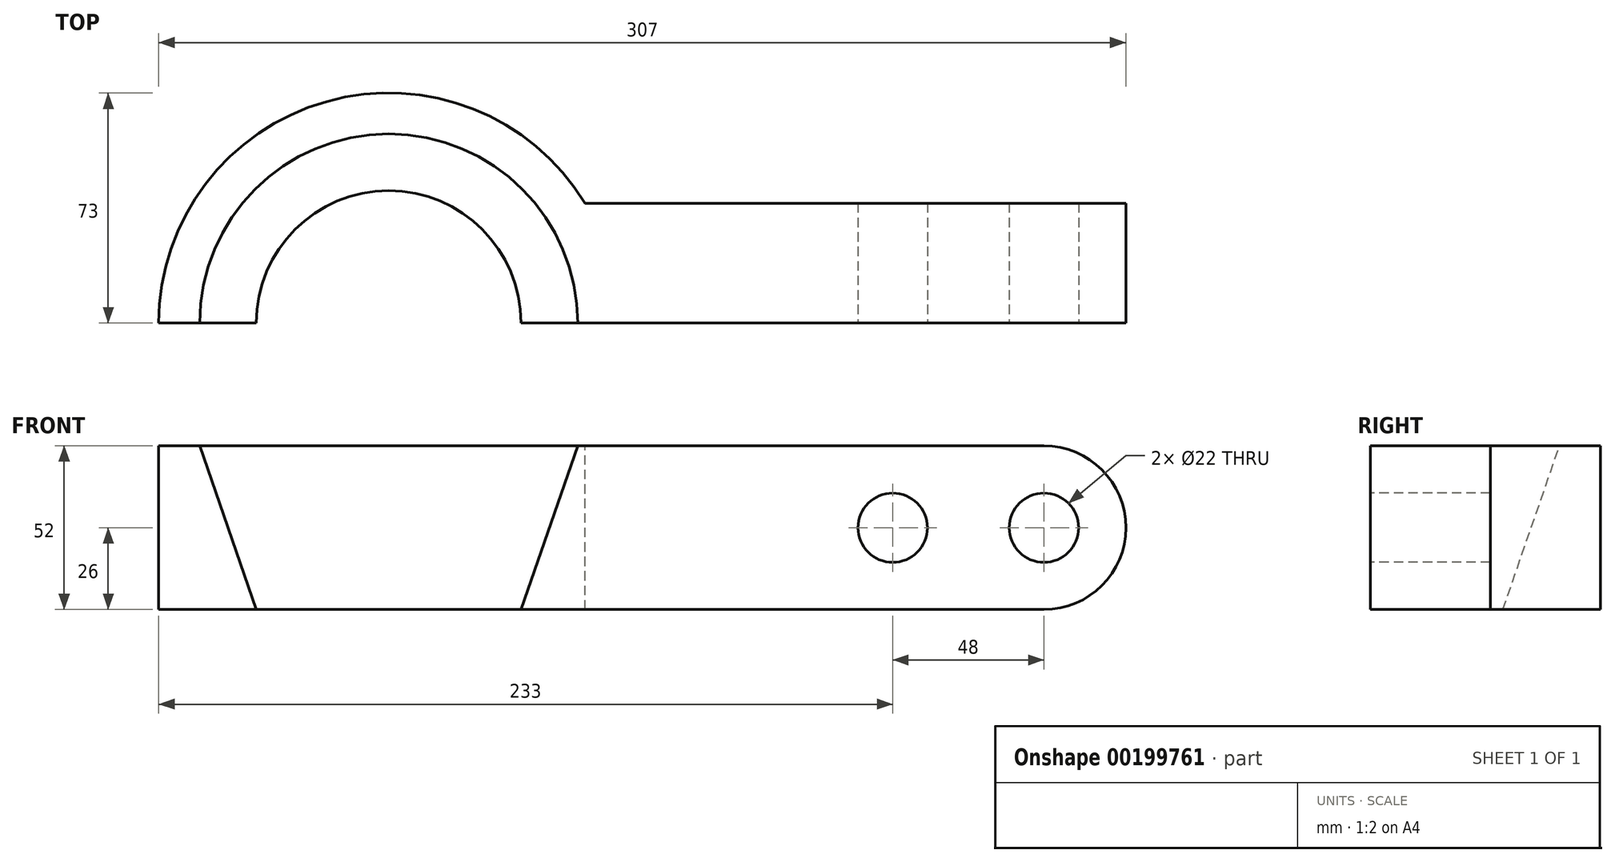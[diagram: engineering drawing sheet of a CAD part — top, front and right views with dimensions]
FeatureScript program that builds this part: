
annotation { "Feature Type Name" : "Feature", "Feature Type Description" : "" }
export const myFeature = defineFeature(function(context is Context, id is Id, definition is map)
    precondition{}
    {
        {
            var Q0;
            Q0=qCreatedBy(makeId("Front.planeOp"),FACE);
            var sketch = newSketch(context, id + "F0", { "sketchPlane" : qUnion([Q0])});
            skLineSegment(sketch, "E0", {"start": v(-73, 0) * mm, "end": v(-73, 52) * mm});
            skLineSegment(sketch, "E1", {"start": v(-73, 52) * mm, "end": v(-60, 52) * mm});
            skLineSegment(sketch, "E2", {"start": v(-60, 52) * mm, "end": v(-42, 0) * mm});
            skLineSegment(sketch, "E3", {"start": v(-42, 0) * mm, "end": v(-73, 0) * mm});
            skLineSegment(sketch, "E4", {"start": v(0, 0) * mm, "end": v(0, 74.37) * mm, "construction": true});
            skSolve(sketch);
        }
        {
            var Q0;
            Q0=qCreatedBy(makeId("Front.planeOp"),FACE);
            var sketch = newSketch(context, id + "F1", { "sketchPlane" : qUnion([Q0])});
            skLineSegment(sketch, "E5", {"start": v(0, 0) * mm, "end": v(0, 72.86) * mm});
            skSolve(sketch);
        }
        {
            var Q0;
            Q0=makeQuery(id+"F0.imprint","IMPRINT",FACE,{"disambiguationData":[TD([[makeQuery(id+"F0.imprint","IMPRINT",EDGE,{"derivedFrom":sQuery(id+"F0.wireOp",EDGE,"E0")}),-1.0]])]});
            var Q1;
            Q1=sQuery(id+"F1.wireOp",EDGE,"E5");
            revolve(context, id + "F2", {"entities" : qUnion([Q0]), "axis" : qUnion([Q1]), "revolveType" : RevolveType.ONE_DIRECTION, "oppositeDirection" : true, "angle" : 180 * degree});
        }
        {
            var Q0;
            Q0=makeQuery(id+"F2.opRevolve","CAP_FACE",FACE,{"disambiguationData":[OSD([sQuery(id+"F0.wireOp",EDGE,"E0"),sQuery(id+"F0.wireOp",EDGE,"E1"),sQuery(id+"F0.wireOp",EDGE,"E2"),sQuery(id+"F0.wireOp",EDGE,"E3")])],"isStart":false});
            var sketch = newSketch(context, id + "F3", { "sketchPlane" : qUnion([Q0])});
            skLineSegment(sketch, "E6", {"start": v(42, 0) * mm, "end": v(208, 0) * mm});
            skLineSegment(sketch, "E7", {"start": v(208, 52) * mm, "end": v(60, 52) * mm});
            skArc(sketch, "E8", {"start": v(208, 0) * mm, "mid": v(234, 26) * mm, "end": v(208, 52) * mm});
            skCircle(sketch, "E9", {"center": v(160, 26) * mm, "radius": 11 * mm});
            skCircle(sketch, "E10", {"center": v(208, 26) * mm, "radius": 11 * mm});
            skLineSegment(sketch, "E11", {"start": v(160, 26) * mm, "end": v(208, 26) * mm, "construction": true});
            skLineSegment(sketch, "E12", {"start": v(60, 52) * mm, "end": v(42, 0) * mm});
            skSolve(sketch);
        }
        {
            var Q0;
            {var subQ0=sQuery(id+"F3.wireOp",EDGE,"E8");Q0=makeQuery(id+"F3.imprint","IMPRINT",FACE,{"disambiguationData":[TD([[makeQuery(id+"F3.imprint","IMPRINT",EDGE,{"derivedFrom":subQ0}),1.0]])]});}
            var Q1;
            {var subQ2=sQuery(id+"F3.wireOp",EDGE,"E12");Q1=makeQuery(id+"F3.imprint","IMPRINT",FACE,{"disambiguationData":[TD([[makeQuery(id+"F3.imprint","IMPRINT",EDGE,{"derivedFrom":subQ2}),1.0]])]});}
            extrude(context, id + "F4", {"entities" : qUnion([Q0, Q1]), "operationType" : NewBodyOperationType.ADD, "oppositeDirection" : true, "depth" : 38 * mm});
        }
    });
